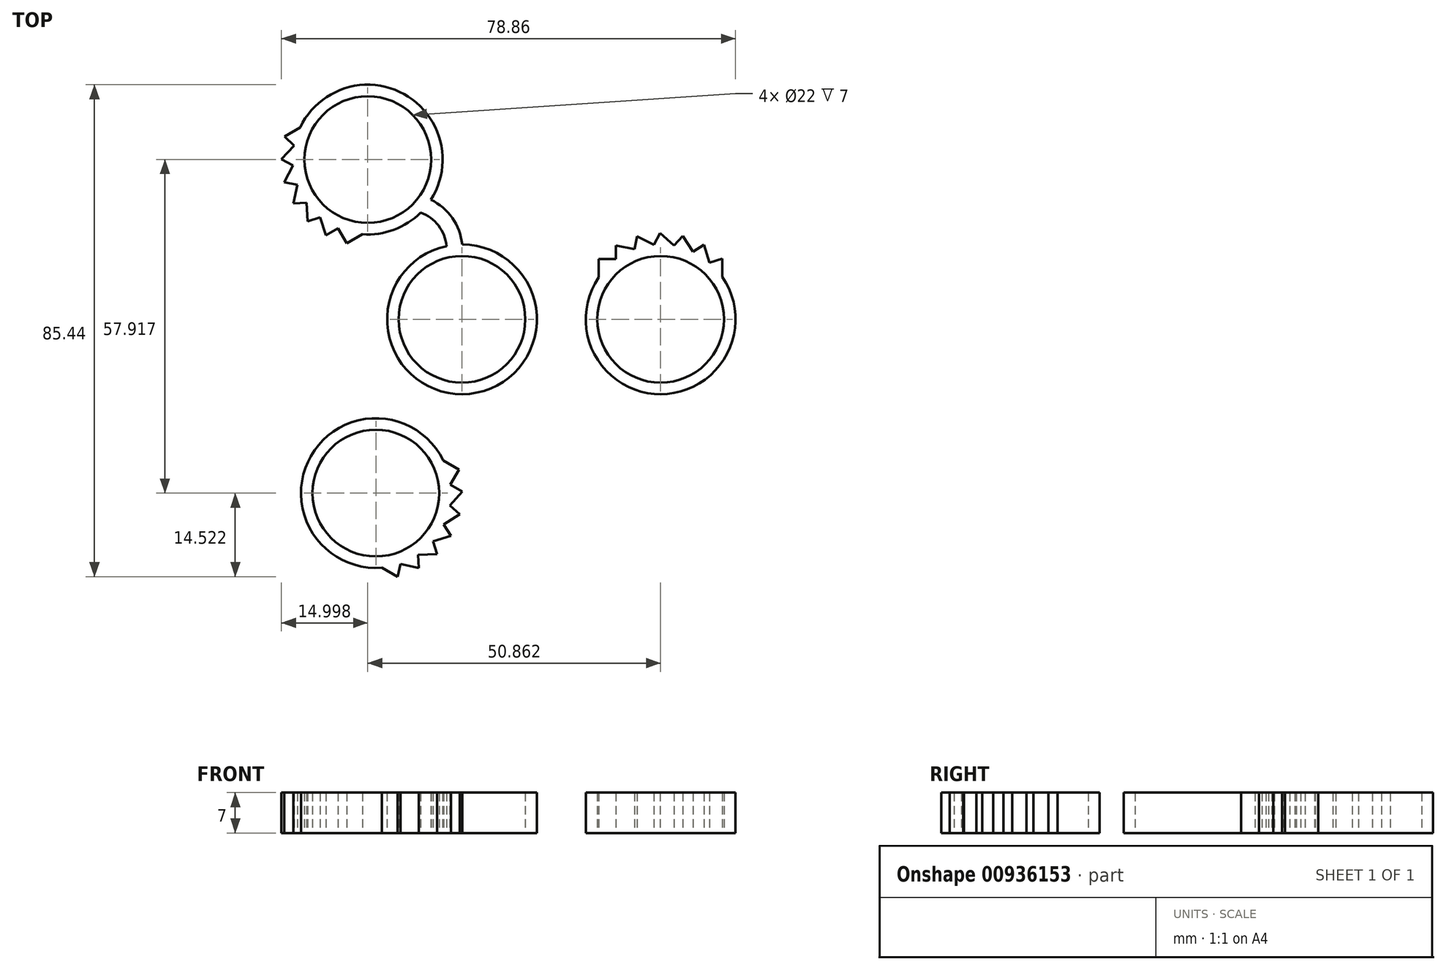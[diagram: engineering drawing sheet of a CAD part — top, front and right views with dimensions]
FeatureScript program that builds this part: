
annotation { "Feature Type Name" : "Feature", "Feature Type Description" : "" }
export const myFeature = defineFeature(function(context is Context, id is Id, definition is map)
    precondition{}
    {
        {
            var Q0;
            Q0=qCreatedBy(makeId("Top.planeOp"),FACE);
            var sketch = newSketch(context, id + "F0", { "sketchPlane" : qUnion([Q0])});
            skCircle(sketch, "E0", {"center": v(0, 0) * mm, "radius": 11 * mm});
            skCircle(sketch, "E1", {"center": v(34.5, 0) * mm, "radius": 11 * mm});
            skCircle(sketch, "E2.1.0", {"center": v(-16.36, 27.74) * mm, "radius": 11 * mm});
            skCircle(sketch, "E2.2.0", {"center": v(-14.95, -30.18) * mm, "radius": 11 * mm});
            skPoint(sketch, "E2.center", {"position": v(1.06, -0.81) * mm});
            skArc(sketch, "E3", {"start": v(0.03, 13) * mm, "mid": v(-1.65, 17.6) * mm, "end": v(-5.4, 20.76) * mm});
            skArc(sketch, "E4", {"start": v(-7.18, 18.53) * mm, "mid": v(-4.09, 16.28) * mm, "end": v(-2.7, 12.72) * mm});
            skPoint(sketch, "E5.center", {"position": v(4.5, 0) * mm});
            skCircle(sketch, "E6", {"center": v(-16.36, 27.74) * mm, "radius": 13 * mm});
            skPoint(sketch, "E7.orphan", {"position": v(-9.78, 18.92) * mm});
            skPoint(sketch, "E8.orphan", {"position": v(-7.34, 21.44) * mm});
            skCircle(sketch, "E9.1.0", {"center": v(-14.95, -30.18) * mm, "radius": 13 * mm});
            skCircle(sketch, "E9.2.0", {"center": v(34.5, 0) * mm, "radius": 13 * mm});
            skArc(sketch, "E9.2.2", {"start": v(21.94, -3.35) * mm, "mid": v(17.4, -4.96) * mm, "end": v(12.92, -3.14) * mm});
            skCircle(sketch, "E10", {"center": v(0, 0) * mm, "radius": 13 * mm});
            skArc(sketch, "E11", {"start": v(21.39, 7.28) * mm, "mid": v(34.5, 15) * mm, "end": v(47.61, 7.28) * mm});
            skLineSegment(sketch, "E12", {"start": v(21.39, 7.28) * mm, "end": v(47.61, 7.28) * mm});
            skLineSegment(sketch, "E13", {"start": v(21.39, 7.28) * mm, "end": v(23.73, 7.28) * mm});
            skLineSegment(sketch, "E14", {"start": v(23.73, 7.28) * mm, "end": v(23.73, 10.44) * mm});
            skLineSegment(sketch, "E15", {"start": v(23.73, 10.44) * mm, "end": v(26.76, 10.44) * mm});
            skLineSegment(sketch, "E16", {"start": v(26.76, 10.44) * mm, "end": v(26.76, 12.85) * mm});
            skLineSegment(sketch, "E17", {"start": v(26.76, 12.85) * mm, "end": v(29.96, 12.18) * mm});
            skLineSegment(sketch, "E18", {"start": v(29.96, 12.18) * mm, "end": v(30.43, 14.44) * mm});
            skLineSegment(sketch, "E19", {"start": v(30.43, 14.44) * mm, "end": v(33.34, 12.95) * mm});
            skLineSegment(sketch, "E20", {"start": v(33.34, 12.95) * mm, "end": v(34.39, 15) * mm});
            skLineSegment(sketch, "E21", {"start": v(34.39, 15) * mm, "end": v(36.8, 12.8) * mm});
            skLineSegment(sketch, "E22", {"start": v(36.8, 12.8) * mm, "end": v(38.36, 14.5) * mm});
            skLineSegment(sketch, "E23", {"start": v(38.36, 14.5) * mm, "end": v(40.1, 11.73) * mm});
            skLineSegment(sketch, "E24", {"start": v(40.1, 11.73) * mm, "end": v(42.05, 12.96) * mm});
            skLineSegment(sketch, "E25", {"start": v(42.05, 12.96) * mm, "end": v(43, 9.83) * mm});
            skLineSegment(sketch, "E26", {"start": v(43, 9.83) * mm, "end": v(45.2, 10.5) * mm});
            skLineSegment(sketch, "E27", {"start": v(45.2, 10.5) * mm, "end": v(45.2, 7.37) * mm});
            skPoint(sketch, "E28.end.orphan", {"position": v(46.37, 7.28) * mm});
            skArc(sketch, "E29.1.0", {"start": v(-16.11, 12.74) * mm, "mid": v(-29.35, 20.24) * mm, "end": v(-29.23, 35.45) * mm});
            skLineSegment(sketch, "E29.1.1", {"start": v(-16.11, 12.74) * mm, "end": v(-17.28, 14.77) * mm});
            skLineSegment(sketch, "E29.1.2", {"start": v(-17.28, 14.77) * mm, "end": v(-20.02, 13.2) * mm});
            skLineSegment(sketch, "E29.1.3", {"start": v(-16.11, 12.74) * mm, "end": v(-29.23, 35.45) * mm});
            skLineSegment(sketch, "E29.1.4", {"start": v(-20.02, 13.2) * mm, "end": v(-21.53, 15.81) * mm});
            skLineSegment(sketch, "E29.1.5", {"start": v(-21.53, 15.81) * mm, "end": v(-23.62, 14.6) * mm});
            skLineSegment(sketch, "E29.1.6", {"start": v(-23.62, 14.6) * mm, "end": v(-24.64, 17.71) * mm});
            skLineSegment(sketch, "E29.1.7", {"start": v(-24.64, 17.71) * mm, "end": v(-26.83, 17) * mm});
            skLineSegment(sketch, "E29.1.8", {"start": v(-26.83, 17) * mm, "end": v(-27, 20.26) * mm});
            skLineSegment(sketch, "E29.1.9", {"start": v(-27, 20.26) * mm, "end": v(-29.3, 20.14) * mm});
            skLineSegment(sketch, "E29.1.10", {"start": v(-29.3, 20.14) * mm, "end": v(-28.6, 23.33) * mm});
            skLineSegment(sketch, "E29.1.11", {"start": v(-28.6, 23.33) * mm, "end": v(-30.84, 23.83) * mm});
            skLineSegment(sketch, "E29.1.12", {"start": v(-30.84, 23.83) * mm, "end": v(-29.32, 26.72) * mm});
            skLineSegment(sketch, "E29.1.13", {"start": v(-29.32, 26.72) * mm, "end": v(-31.36, 27.8) * mm});
            skLineSegment(sketch, "E29.1.14", {"start": v(-31.36, 27.8) * mm, "end": v(-29.13, 30.19) * mm});
            skLineSegment(sketch, "E29.1.15", {"start": v(-29.13, 30.19) * mm, "end": v(-30.81, 31.76) * mm});
            skLineSegment(sketch, "E29.1.16", {"start": v(-30.81, 31.76) * mm, "end": v(-28.1, 33.32) * mm});
            skArc(sketch, "E29.2.0", {"start": v(-2.09, -22.46) * mm, "mid": v(-1.96, -37.68) * mm, "end": v(-15.2, -45.18) * mm});
            skLineSegment(sketch, "E29.2.1", {"start": v(-2.09, -22.46) * mm, "end": v(-3.26, -24.5) * mm});
            skLineSegment(sketch, "E29.2.2", {"start": v(-3.26, -24.5) * mm, "end": v(-0.53, -26.07) * mm});
            skLineSegment(sketch, "E29.2.3", {"start": v(-2.09, -22.46) * mm, "end": v(-15.2, -45.18) * mm});
            skLineSegment(sketch, "E29.2.4", {"start": v(-0.53, -26.07) * mm, "end": v(-2.04, -28.7) * mm});
            skLineSegment(sketch, "E29.2.5", {"start": v(-2.04, -28.7) * mm, "end": v(0.04, -29.9) * mm});
            skLineSegment(sketch, "E29.2.6", {"start": v(0.04, -29.9) * mm, "end": v(-2.13, -32.34) * mm});
            skLineSegment(sketch, "E29.2.7", {"start": v(-2.13, -32.34) * mm, "end": v(-0.41, -33.87) * mm});
            skLineSegment(sketch, "E29.2.8", {"start": v(-0.41, -33.87) * mm, "end": v(-3.16, -35.65) * mm});
            skLineSegment(sketch, "E29.2.9", {"start": v(-3.16, -35.65) * mm, "end": v(-1.9, -37.58) * mm});
            skLineSegment(sketch, "E29.2.10", {"start": v(-1.9, -37.58) * mm, "end": v(-5.02, -38.57) * mm});
            skLineSegment(sketch, "E29.2.11", {"start": v(-5.02, -38.57) * mm, "end": v(-4.33, -40.77) * mm});
            skLineSegment(sketch, "E29.2.12", {"start": v(-4.33, -40.77) * mm, "end": v(-7.6, -40.9) * mm});
            skLineSegment(sketch, "E29.2.13", {"start": v(-7.6, -40.9) * mm, "end": v(-7.5, -43.2) * mm});
            skLineSegment(sketch, "E29.2.14", {"start": v(-7.5, -43.2) * mm, "end": v(-10.69, -42.46) * mm});
            skLineSegment(sketch, "E29.2.15", {"start": v(-10.69, -42.46) * mm, "end": v(-11.2, -44.7) * mm});
            skLineSegment(sketch, "E29.2.16", {"start": v(-11.2, -44.7) * mm, "end": v(-13.92, -43.14) * mm});
            skArc(sketch, "E30", {"start": v(-28.1, 33.32) * mm, "mid": v(-27.6, 21.2) * mm, "end": v(-17.28, 14.77) * mm});
            skCircle(sketch, "E31", {"center": v(-16.36, 27.74) * mm, "radius": 1.7 * mm});
            skArc(sketch, "E32", {"start": v(21.94, -3.35) * mm, "mid": v(17.22, -4.95) * mm, "end": v(12.67, -2.9) * mm});
            skArc(sketch, "E33", {"start": v(22.97, -6.01) * mm, "mid": v(17.3, -7.5) * mm, "end": v(11.86, -5.33) * mm});
            skPoint(sketch, "E34.orphan", {"position": v(-14.4, -17.2) * mm});
            skPoint(sketch, "E35.orphan", {"position": v(-11.57, -17.63) * mm});
            skArc(sketch, "E36", {"start": v(-11.57, -17.63) * mm, "mid": v(-10.96, -13.36) * mm, "end": v(-7.9, -10.32) * mm});
            skArc(sketch, "E37", {"start": v(-14.4, -17.2) * mm, "mid": v(-13.42, -12.15) * mm, "end": v(-9.97, -8.34) * mm});
            skPoint(sketch, "E9.1.2.end.orphan", {"position": v(-6.89, -9.92) * mm});
            skArc(sketch, "E38", {"start": v(-5.4, 20.76) * mm, "mid": v(-1.65, 17.6) * mm, "end": v(0.03, 13) * mm});
            skPoint(sketch, "E39.orphan", {"position": v(-2.85, 10.62) * mm});
            skPoint(sketch, "E40.orphan", {"position": v(0, 11) * mm});
            skSolve(sketch);
        }
        {
            var Q0;
            {var subQ0=sQuery(id+"F0.wireOp",EDGE,"E6");var subQ1=sQuery(id+"F0.wireOp",EDGE,"E3");var subQ2=makeQuery(id+"F0.imprint","INTERSECT",VERTEX,{"derivedFrom":[subQ1,subQ0]});Q0=makeQuery(id+"F0.imprint","IMPRINT",FACE,{"disambiguationData":[TD([[makeQuery(id+"F0.imprint","IMPRINT",EDGE,{"disambiguationData":[TD([[subQ2,1.0]])],"derivedFrom":subQ1}),1.0]])]});}
            var Q1;
            {var subQ0=sQuery(id+"F0.wireOp",EDGE,"E29.1.1");Q1=makeQuery(id+"F0.imprint","IMPRINT",FACE,{"disambiguationData":[TD([[makeQuery(id+"F0.imprint","IMPRINT",EDGE,{"derivedFrom":subQ0}),-1.0]])]});}
            var Q2;
            {var subQ0=sQuery(id+"F0.wireOp",EDGE,"E29.2.1");Q2=makeQuery(id+"F0.imprint","IMPRINT",FACE,{"disambiguationData":[TD([[makeQuery(id+"F0.imprint","IMPRINT",EDGE,{"derivedFrom":subQ0}),-1.0]])]});}
            var Q3;
            {var subQ0=sQuery(id+"F0.wireOp",EDGE,"E13");Q3=makeQuery(id+"F0.imprint","IMPRINT",FACE,{"disambiguationData":[TD([[makeQuery(id+"F0.imprint","IMPRINT",EDGE,{"derivedFrom":subQ0}),-1.0]])]});}
            var Q4;
            {var subQ0=sQuery(id+"F0.wireOp",EDGE,"E4");var subQ1=sQuery(id+"F0.wireOp",EDGE,"E0");var subQ2=makeQuery(id+"F0.imprint","INTERSECT",VERTEX,{"derivedFrom":[subQ1,subQ0]});Q4=makeQuery(id+"F0.imprint","IMPRINT",FACE,{"disambiguationData":[TD([[makeQuery(id+"F0.imprint","IMPRINT",EDGE,{"disambiguationData":[TD([[subQ2,-1.0]])],"derivedFrom":subQ1}),-1.0]])]});}
            var Q5;
            {var subQ0=sQuery(id+"F0.wireOp",EDGE,"E9.1.2");var subQ1=sQuery(id+"F0.wireOp",EDGE,"E0");var subQ2=makeQuery(id+"F0.imprint","INTERSECT",VERTEX,{"derivedFrom":[subQ1,subQ0]});Q5=makeQuery(id+"F0.imprint","IMPRINT",FACE,{"disambiguationData":[TD([[makeQuery(id+"F0.imprint","IMPRINT",EDGE,{"disambiguationData":[TD([[subQ2,-1.0]])],"derivedFrom":subQ1}),-1.0]])]});}
            var Q6;
            {var subQ0=sQuery(id+"F0.wireOp",EDGE,"E3");var subQ1=sQuery(id+"F0.wireOp",EDGE,"E0");var subQ2=makeQuery(id+"F0.imprint","INTERSECT",VERTEX,{"derivedFrom":[subQ1,subQ0]});Q6=makeQuery(id+"F0.imprint","IMPRINT",FACE,{"disambiguationData":[TD([[makeQuery(id+"F0.imprint","IMPRINT",EDGE,{"disambiguationData":[TD([[subQ2,1.0]])],"derivedFrom":subQ1}),-1.0]])]});}
            var Q7;
            {var subQ2=sQuery(id+"F0.wireOp",EDGE,"E29.1.3");var subQ6=sQuery(id+"F0.wireOp",EDGE,"E2.1.0");var subQ7=makeQuery(id+"F0.imprint","INTERSECT",VERTEX,{"disambiguationData":[OD(0.0)],"derivedFrom":[subQ6,subQ2]});Q7=makeQuery(id+"F0.imprint","IMPRINT",FACE,{"disambiguationData":[TD([[makeQuery(id+"F0.imprint","IMPRINT",EDGE,{"disambiguationData":[TD([[subQ7,-1.0]])],"derivedFrom":subQ6}),-1.0]])]});}
            var Q8;
            {var subQ2=sQuery(id+"F0.wireOp",EDGE,"E29.2.3");var subQ6=sQuery(id+"F0.wireOp",EDGE,"E2.2.0");var subQ7=makeQuery(id+"F0.imprint","INTERSECT",VERTEX,{"disambiguationData":[OD(0.0)],"derivedFrom":[subQ6,subQ2]});Q8=makeQuery(id+"F0.imprint","IMPRINT",FACE,{"disambiguationData":[TD([[makeQuery(id+"F0.imprint","IMPRINT",EDGE,{"disambiguationData":[TD([[subQ7,-1.0]])],"derivedFrom":subQ6}),-1.0]])]});}
            var Q9;
            {var subQ0=sQuery(id+"F0.wireOp",EDGE,"E29.1.15");Q9=makeQuery(id+"F0.imprint","IMPRINT",FACE,{"disambiguationData":[TD([[makeQuery(id+"F0.imprint","IMPRINT",EDGE,{"derivedFrom":subQ0}),-1.0]])]});}
            var Q10;
            {var subQ0=sQuery(id+"F0.wireOp",EDGE,"E29.1.13");Q10=makeQuery(id+"F0.imprint","IMPRINT",FACE,{"disambiguationData":[TD([[makeQuery(id+"F0.imprint","IMPRINT",EDGE,{"derivedFrom":subQ0}),-1.0]])]});}
            var Q11;
            {var subQ0=sQuery(id+"F0.wireOp",EDGE,"E29.1.11");Q11=makeQuery(id+"F0.imprint","IMPRINT",FACE,{"disambiguationData":[TD([[makeQuery(id+"F0.imprint","IMPRINT",EDGE,{"derivedFrom":subQ0}),-1.0]])]});}
            var Q12;
            {var subQ0=sQuery(id+"F0.wireOp",EDGE,"E29.1.9");Q12=makeQuery(id+"F0.imprint","IMPRINT",FACE,{"disambiguationData":[TD([[makeQuery(id+"F0.imprint","IMPRINT",EDGE,{"derivedFrom":subQ0}),-1.0]])]});}
            var Q13;
            {var subQ0=sQuery(id+"F0.wireOp",EDGE,"E29.1.7");Q13=makeQuery(id+"F0.imprint","IMPRINT",FACE,{"disambiguationData":[TD([[makeQuery(id+"F0.imprint","IMPRINT",EDGE,{"derivedFrom":subQ0}),-1.0]])]});}
            var Q14;
            {var subQ0=sQuery(id+"F0.wireOp",EDGE,"E29.1.5");Q14=makeQuery(id+"F0.imprint","IMPRINT",FACE,{"disambiguationData":[TD([[makeQuery(id+"F0.imprint","IMPRINT",EDGE,{"derivedFrom":subQ0}),-1.0]])]});}
            var Q15;
            {var subQ0=sQuery(id+"F0.wireOp",EDGE,"E29.1.2");Q15=makeQuery(id+"F0.imprint","IMPRINT",FACE,{"disambiguationData":[TD([[makeQuery(id+"F0.imprint","IMPRINT",EDGE,{"derivedFrom":subQ0}),-1.0]])]});}
            var Q16;
            {var subQ0=sQuery(id+"F0.wireOp",EDGE,"E29.2.15");Q16=makeQuery(id+"F0.imprint","IMPRINT",FACE,{"disambiguationData":[TD([[makeQuery(id+"F0.imprint","IMPRINT",EDGE,{"derivedFrom":subQ0}),-1.0]])]});}
            var Q17;
            {var subQ0=sQuery(id+"F0.wireOp",EDGE,"E29.2.13");Q17=makeQuery(id+"F0.imprint","IMPRINT",FACE,{"disambiguationData":[TD([[makeQuery(id+"F0.imprint","IMPRINT",EDGE,{"derivedFrom":subQ0}),-1.0]])]});}
            var Q18;
            {var subQ0=sQuery(id+"F0.wireOp",EDGE,"E29.2.11");Q18=makeQuery(id+"F0.imprint","IMPRINT",FACE,{"disambiguationData":[TD([[makeQuery(id+"F0.imprint","IMPRINT",EDGE,{"derivedFrom":subQ0}),-1.0]])]});}
            var Q19;
            {var subQ0=sQuery(id+"F0.wireOp",EDGE,"E29.2.9");Q19=makeQuery(id+"F0.imprint","IMPRINT",FACE,{"disambiguationData":[TD([[makeQuery(id+"F0.imprint","IMPRINT",EDGE,{"derivedFrom":subQ0}),-1.0]])]});}
            var Q20;
            {var subQ0=sQuery(id+"F0.wireOp",EDGE,"E29.2.7");Q20=makeQuery(id+"F0.imprint","IMPRINT",FACE,{"disambiguationData":[TD([[makeQuery(id+"F0.imprint","IMPRINT",EDGE,{"derivedFrom":subQ0}),-1.0]])]});}
            var Q21;
            {var subQ0=sQuery(id+"F0.wireOp",EDGE,"E29.2.5");Q21=makeQuery(id+"F0.imprint","IMPRINT",FACE,{"disambiguationData":[TD([[makeQuery(id+"F0.imprint","IMPRINT",EDGE,{"derivedFrom":subQ0}),-1.0]])]});}
            var Q22;
            {var subQ0=sQuery(id+"F0.wireOp",EDGE,"E29.2.2");Q22=makeQuery(id+"F0.imprint","IMPRINT",FACE,{"disambiguationData":[TD([[makeQuery(id+"F0.imprint","IMPRINT",EDGE,{"derivedFrom":subQ0}),-1.0]])]});}
            var Q23;
            {var subQ0=sQuery(id+"F0.wireOp",EDGE,"E26");Q23=makeQuery(id+"F0.imprint","IMPRINT",FACE,{"disambiguationData":[TD([[makeQuery(id+"F0.imprint","IMPRINT",EDGE,{"derivedFrom":subQ0}),-1.0]])]});}
            var Q24;
            {var subQ0=sQuery(id+"F0.wireOp",EDGE,"E24");Q24=makeQuery(id+"F0.imprint","IMPRINT",FACE,{"disambiguationData":[TD([[makeQuery(id+"F0.imprint","IMPRINT",EDGE,{"derivedFrom":subQ0}),-1.0]])]});}
            var Q25;
            {var subQ0=sQuery(id+"F0.wireOp",EDGE,"E22");Q25=makeQuery(id+"F0.imprint","IMPRINT",FACE,{"disambiguationData":[TD([[makeQuery(id+"F0.imprint","IMPRINT",EDGE,{"derivedFrom":subQ0}),-1.0]])]});}
            var Q26;
            {var subQ0=sQuery(id+"F0.wireOp",EDGE,"E20");Q26=makeQuery(id+"F0.imprint","IMPRINT",FACE,{"disambiguationData":[TD([[makeQuery(id+"F0.imprint","IMPRINT",EDGE,{"derivedFrom":subQ0}),-1.0]])]});}
            var Q27;
            {var subQ0=sQuery(id+"F0.wireOp",EDGE,"E18");Q27=makeQuery(id+"F0.imprint","IMPRINT",FACE,{"disambiguationData":[TD([[makeQuery(id+"F0.imprint","IMPRINT",EDGE,{"derivedFrom":subQ0}),-1.0]])]});}
            var Q28;
            {var subQ0=sQuery(id+"F0.wireOp",EDGE,"E16");Q28=makeQuery(id+"F0.imprint","IMPRINT",FACE,{"disambiguationData":[TD([[makeQuery(id+"F0.imprint","IMPRINT",EDGE,{"derivedFrom":subQ0}),-1.0]])]});}
            var Q29;
            {var subQ0=sQuery(id+"F0.wireOp",EDGE,"E14");Q29=makeQuery(id+"F0.imprint","IMPRINT",FACE,{"disambiguationData":[TD([[makeQuery(id+"F0.imprint","IMPRINT",EDGE,{"derivedFrom":subQ0}),-1.0]])]});}
            var Q30;
            {var subQ0=sQuery(id+"F0.wireOp",EDGE,"E3");var subQ1=sQuery(id+"F0.wireOp",EDGE,"E0");var subQ2=makeQuery(id+"F0.imprint","INTERSECT",VERTEX,{"derivedFrom":[subQ1,subQ0]});Q30=makeQuery(id+"F0.imprint","IMPRINT",FACE,{"disambiguationData":[TD([[makeQuery(id+"F0.imprint","IMPRINT",EDGE,{"disambiguationData":[TD([[subQ2,-1.0]])],"derivedFrom":subQ1}),-1.0]])]});}
            var Q31;
            {var subQ0=sQuery(id+"F0.wireOp",EDGE,"E9.1.1");var subQ1=sQuery(id+"F0.wireOp",EDGE,"E0");var subQ2=makeQuery(id+"F0.imprint","INTERSECT",VERTEX,{"derivedFrom":[subQ1,subQ0]});Q31=makeQuery(id+"F0.imprint","IMPRINT",FACE,{"disambiguationData":[TD([[makeQuery(id+"F0.imprint","IMPRINT",EDGE,{"disambiguationData":[TD([[subQ2,-1.0]])],"derivedFrom":subQ1}),-1.0]])]});}
            var Q32;
            {var subQ0=sQuery(id+"F0.wireOp",EDGE,"E9.2.1");var subQ1=sQuery(id+"F0.wireOp",EDGE,"E0");var subQ2=makeQuery(id+"F0.imprint","INTERSECT",VERTEX,{"derivedFrom":[subQ1,subQ0]});Q32=makeQuery(id+"F0.imprint","IMPRINT",FACE,{"disambiguationData":[TD([[makeQuery(id+"F0.imprint","IMPRINT",EDGE,{"disambiguationData":[TD([[subQ2,-1.0]])],"derivedFrom":subQ1}),-1.0]])]});}
            var Q33;
            {var subQ2=sQuery(id+"F0.wireOp",EDGE,"E12");var subQ4=sQuery(id+"F0.wireOp",EDGE,"E1");var subQ5=makeQuery(id+"F0.imprint","INTERSECT",VERTEX,{"disambiguationData":[OD(0.0)],"derivedFrom":[subQ4,subQ2]});Q33=makeQuery(id+"F0.imprint","IMPRINT",FACE,{"disambiguationData":[TD([[makeQuery(id+"F0.imprint","IMPRINT",EDGE,{"disambiguationData":[TD([[subQ5,1.0]])],"derivedFrom":subQ4}),-1.0]])]});}
            var Q34;
            {var subQ2=sQuery(id+"F0.wireOp",EDGE,"E29.1.3");var subQ9=sQuery(id+"F0.wireOp",EDGE,"E2.1.0");var subQ10=makeQuery(id+"F0.imprint","INTERSECT",VERTEX,{"disambiguationData":[OD(0.0)],"derivedFrom":[subQ9,subQ2]});Q34=makeQuery(id+"F0.imprint","IMPRINT",FACE,{"disambiguationData":[TD([[makeQuery(id+"F0.imprint","IMPRINT",EDGE,{"disambiguationData":[TD([[subQ10,1.0]])],"derivedFrom":subQ9}),-1.0]])]});}
            var Q35;
            {var subQ2=sQuery(id+"F0.wireOp",EDGE,"E29.2.3");var subQ7=sQuery(id+"F0.wireOp",EDGE,"E2.2.0");var subQ8=makeQuery(id+"F0.imprint","INTERSECT",VERTEX,{"disambiguationData":[OD(0.0)],"derivedFrom":[subQ7,subQ2]});Q35=makeQuery(id+"F0.imprint","IMPRINT",FACE,{"disambiguationData":[TD([[makeQuery(id+"F0.imprint","IMPRINT",EDGE,{"disambiguationData":[TD([[subQ8,1.0]])],"derivedFrom":subQ7}),-1.0]])]});}
            var Q36;
            {var subQ0=sQuery(id+"F0.wireOp",EDGE,"E9.2.0");var subQ1=makeQuery(id+"F0.imprint","IMPRINT",VERTEX,{"disambiguationData":[OD(0.0)],"derivedFrom":subQ0});Q36=makeQuery(id+"F0.imprint","IMPRINT",FACE,{"disambiguationData":[TD([[makeQuery(id+"F0.imprint","IMPRINT",EDGE,{"disambiguationData":[TD([[subQ1,1.0]])],"derivedFrom":subQ0}),1.0]])]});}
            var Q37;
            {var subQ2=sQuery(id+"F0.wireOp",EDGE,"E12");var subQ6=sQuery(id+"F0.wireOp",EDGE,"E1");var subQ7=makeQuery(id+"F0.imprint","INTERSECT",VERTEX,{"disambiguationData":[OD(0.0)],"derivedFrom":[subQ6,subQ2]});Q37=makeQuery(id+"F0.imprint","IMPRINT",FACE,{"disambiguationData":[TD([[makeQuery(id+"F0.imprint","IMPRINT",EDGE,{"disambiguationData":[TD([[subQ7,-1.0]])],"derivedFrom":subQ6}),-1.0]])]});}
            var Q38;
            {var subQ3=sQuery(id+"F0.wireOp",EDGE,"E33");Q38=makeQuery(id+"F0.imprint","IMPRINT",FACE,{"disambiguationData":[TD([[makeQuery(id+"F0.imprint","IMPRINT",EDGE,{"derivedFrom":subQ3}),-1.0]])]});}
            var Q39;
            {var subQ0=sQuery(id+"F0.wireOp",EDGE,"E4");Q39=makeQuery(id+"F0.imprint","IMPRINT",FACE,{"disambiguationData":[TD([[makeQuery(id+"F0.imprint","IMPRINT",EDGE,{"derivedFrom":subQ0}),1.0]])]});}
            var Q40;
            {var subQ0=sQuery(id+"F0.wireOp",EDGE,"E36");Q40=makeQuery(id+"F0.imprint","IMPRINT",FACE,{"disambiguationData":[TD([[makeQuery(id+"F0.imprint","IMPRINT",EDGE,{"derivedFrom":subQ0}),1.0]])]});}
            extrude(context, id + "F1", {"entities" : qUnion([Q0, Q1, Q2, Q3, Q4, Q5, Q6, Q7, Q8, Q9, Q10, Q11, Q12, Q13, Q14, Q15, Q16, Q17, Q18, Q19, Q20, Q21, Q22, Q23, Q24, Q25, Q26, Q27, Q28, Q29, Q30, Q31, Q32, Q33, Q34, Q35, Q36, Q37, Q38, Q39, Q40]), "depth" : 7 * mm, "offsetDistance" : 25 * mm});
        }
    });
